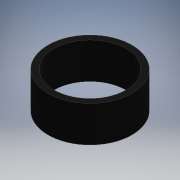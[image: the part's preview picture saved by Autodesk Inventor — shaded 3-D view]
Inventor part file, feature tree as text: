
AUTODESK INVENTOR PART (.ipt)
format: ipt  version: 2016 (Build 200138000, 138)  size: 93,696 bytes
history: native  units: mm
features: other x1, extrude x1, sketch x1
ambient origin geometry x8: Origin, YZ Plane, XZ Plane, XY Plane, X Axis, Y Axis, Z Axis, Center Point
bodies: Body1 (feature_tree)
feature tree (3):
  other  "ソリッド1"
  extrude  "押し出し1"  Depth=14.0mm
  sketch  "スケッチ1"
